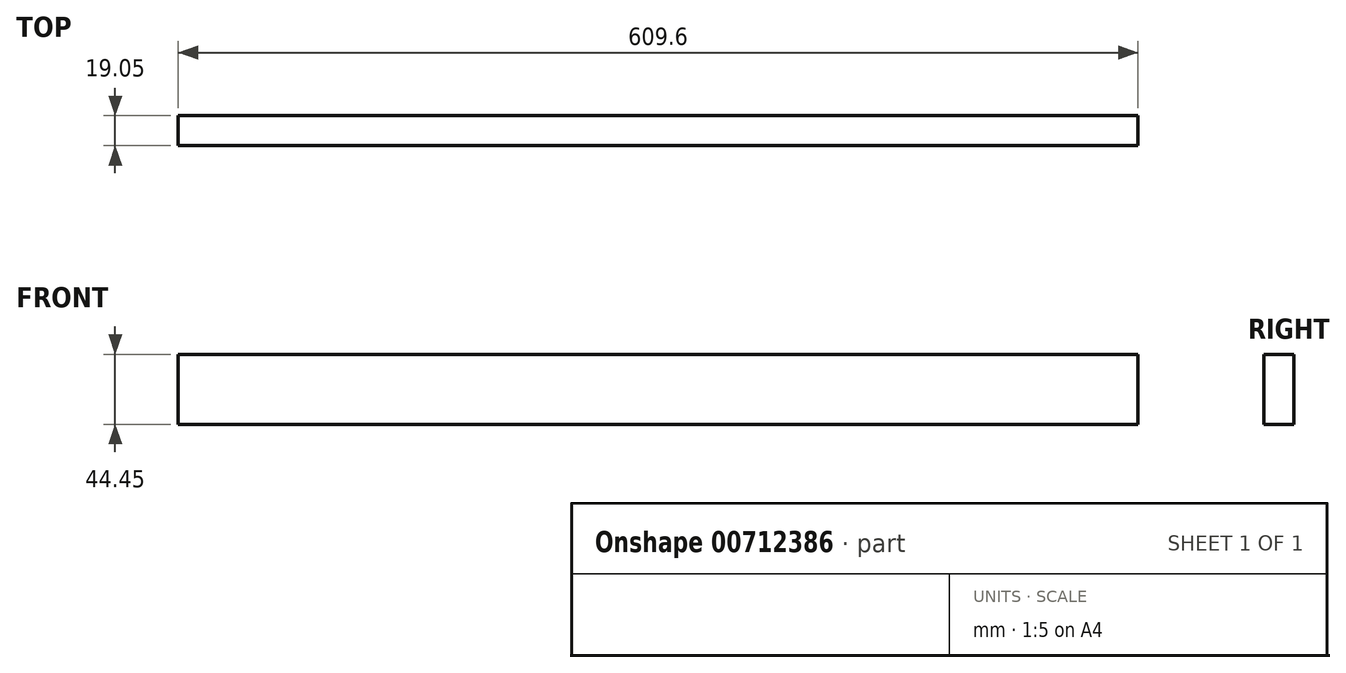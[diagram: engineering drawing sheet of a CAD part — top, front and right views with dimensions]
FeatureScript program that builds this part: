
annotation { "Feature Type Name" : "Feature", "Feature Type Description" : "" }
export const myFeature = defineFeature(function(context is Context, id is Id, definition is map)
    precondition{}
    {
        {
            var Q0;
            Q0=qCreatedBy(makeId("Front.planeOp"),FACE);
            var sketch = newSketch(context, id + "F0", { "sketchPlane" : qUnion([Q0])});
            skLineSegment(sketch, "E0.bottom", {"start": v(0, 0) * mm, "end": v(609.6, 0) * mm});
            skLineSegment(sketch, "E0.top", {"start": v(0, 44.45) * mm, "end": v(609.6, 44.45) * mm});
            skLineSegment(sketch, "E0.left", {"start": v(0, 0) * mm, "end": v(0, 44.45) * mm});
            skLineSegment(sketch, "E0.right", {"start": v(609.6, 0) * mm, "end": v(609.6, 44.45) * mm});
            skSolve(sketch);
        }
        {
            var Q0;
            Q0=makeQuery(id+"F0.imprint","IMPRINT",FACE,{"disambiguationData":[TD([[makeQuery(id+"F0.imprint","IMPRINT",EDGE,{"derivedFrom":sQuery(id+"F0.wireOp",EDGE,"E0.bottom")}),1.0]])]});
            extrude(context, id + "F1", {"entities" : qUnion([Q0]), "depth" : 19.05 * mm, "offsetDistance" : 25.4 * mm});
        }
    });
